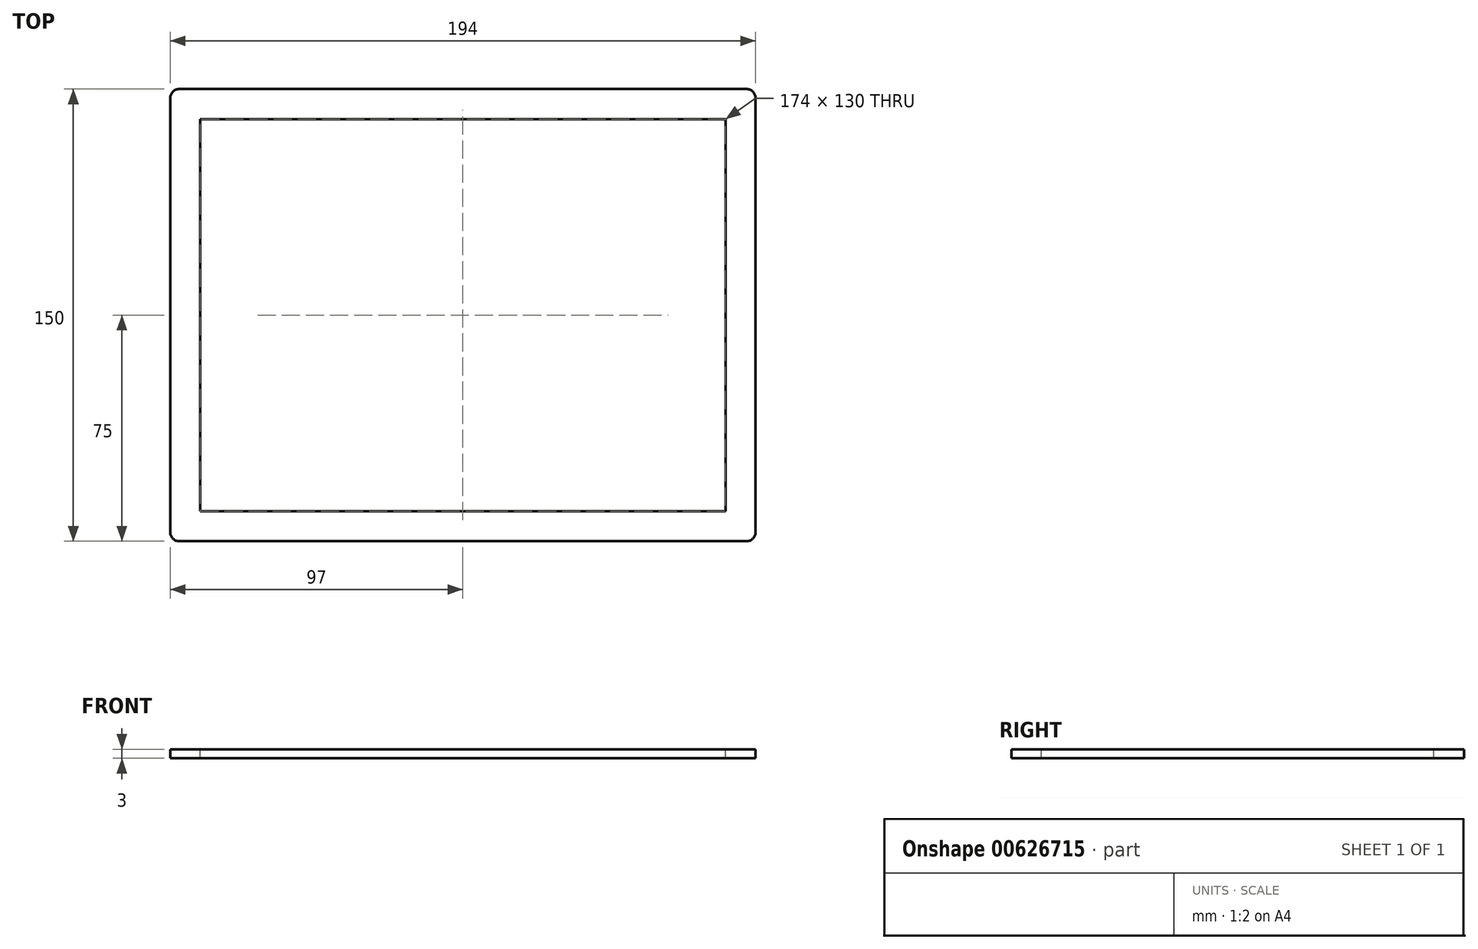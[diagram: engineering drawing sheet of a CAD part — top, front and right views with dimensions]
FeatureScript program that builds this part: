
annotation { "Feature Type Name" : "Feature", "Feature Type Description" : "" }
export const myFeature = defineFeature(function(context is Context, id is Id, definition is map)
    precondition{}
    {
        {
            var Q0;
            Q0=qCreatedBy(makeId("Top.planeOp"),FACE);
            var sketch = newSketch(context, id + "F0", { "sketchPlane" : qUnion([Q0])});
            skLineSegment(sketch, "E0.bottom", {"start": v(97, 75) * mm, "end": v(-97, 75) * mm});
            skLineSegment(sketch, "E0.top", {"start": v(97, -75) * mm, "end": v(-97, -75) * mm});
            skLineSegment(sketch, "E0.left", {"start": v(97, 75) * mm, "end": v(97, -75) * mm});
            skLineSegment(sketch, "E0.right", {"start": v(-97, 75) * mm, "end": v(-97, -75) * mm});
            skPoint(sketch, "E0.middle", {"position": v(0, 0) * mm});
            skSolve(sketch);
        }
        {
            var Q0;
            Q0=makeQuery(id+"F0.imprint","IMPRINT",FACE,{"disambiguationData":[TD([[makeQuery(id+"F0.imprint","IMPRINT",EDGE,{"derivedFrom":sQuery(id+"F0.wireOp",EDGE,"E0.bottom")}),1.0]])]});
            extrude(context, id + "F1", {"entities" : qUnion([Q0]), "depth" : 3 * mm, "offsetDistance" : 25 * mm});
        }
        {
            var Q0;
            Q0=makeQuery(id+"F1.opExtrude","CAP_FACE",FACE,{"disambiguationData":[OSD([sQuery(id+"F0.wireOp",EDGE,"E0.bottom"),sQuery(id+"F0.wireOp",EDGE,"E0.top"),sQuery(id+"F0.wireOp",EDGE,"E0.left"),sQuery(id+"F0.wireOp",EDGE,"E0.right")])],"isStart":false});
            var sketch = newSketch(context, id + "F2", { "sketchPlane" : qUnion([Q0])});
            skLineSegment(sketch, "E1.bottom", {"start": v(87, 65) * mm, "end": v(-87, 65) * mm});
            skLineSegment(sketch, "E1.top", {"start": v(87, -65) * mm, "end": v(-87, -65) * mm});
            skLineSegment(sketch, "E1.left", {"start": v(87, 65) * mm, "end": v(87, -65) * mm});
            skLineSegment(sketch, "E1.right", {"start": v(-87, 65) * mm, "end": v(-87, -65) * mm});
            skPoint(sketch, "E1.middle", {"position": v(0, 0) * mm});
            skSolve(sketch);
        }
        {
            var Q0;
            Q0=makeQuery(id+"F2.imprint","IMPRINT",FACE,{"disambiguationData":[TD([[makeQuery(id+"F2.imprint","IMPRINT",EDGE,{"derivedFrom":sQuery(id+"F2.wireOp",EDGE,"E1.bottom")}),1.0]])]});
            extrude(context, id + "F3", {"entities" : qUnion([Q0]), "operationType" : NewBodyOperationType.REMOVE, "endBound" : BoundingType.UP_TO_NEXT, "oppositeDirection" : true, "depth" : 25 * mm, "offsetDistance" : 25 * mm});
        }
        {
            var Q0;
            Q0=makeQuery(id+"F1.opExtrude","SWEPT_EDGE",EDGE,{"disambiguationData":[OSD([sQuery(id+"F0.wireOp",EDGE,"E0.top"),sQuery(id+"F0.wireOp",EDGE,"E0.right")])]});
            var Q1;
            Q1=makeQuery(id+"F1.opExtrude","SWEPT_EDGE",EDGE,{"disambiguationData":[OSD([sQuery(id+"F0.wireOp",EDGE,"E0.top"),sQuery(id+"F0.wireOp",EDGE,"E0.left")])]});
            var Q2;
            Q2=makeQuery(id+"F1.opExtrude","SWEPT_EDGE",EDGE,{"disambiguationData":[OSD([sQuery(id+"F0.wireOp",EDGE,"E0.bottom"),sQuery(id+"F0.wireOp",EDGE,"E0.left")])]});
            var Q3;
            Q3=makeQuery(id+"F1.opExtrude","SWEPT_EDGE",EDGE,{"disambiguationData":[OSD([sQuery(id+"F0.wireOp",EDGE,"E0.bottom"),sQuery(id+"F0.wireOp",EDGE,"E0.right")])]});
            fillet(context, id + "F4", {"entities" : qUnion([Q0, Q1, Q2, Q3]), "radius" : 3 * mm, "tangentPropagation" : true, "allowEdgeOverflow" : false});
        }
    });
